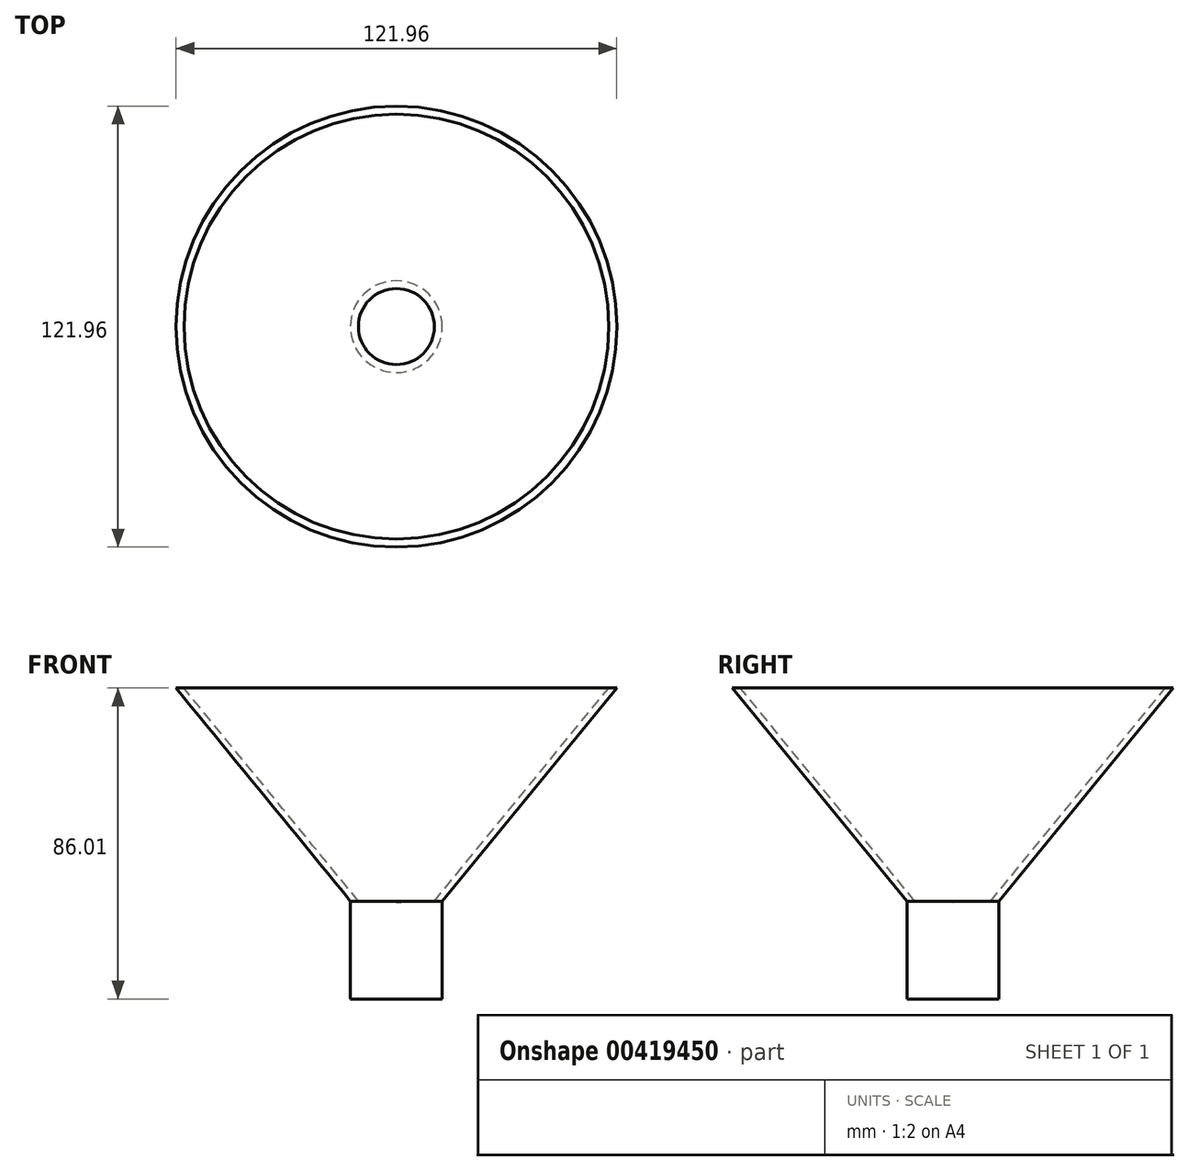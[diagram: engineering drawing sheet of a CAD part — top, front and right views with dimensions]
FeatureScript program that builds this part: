
annotation { "Feature Type Name" : "Feature", "Feature Type Description" : "" }
export const myFeature = defineFeature(function(context is Context, id is Id, definition is map)
    precondition{}
    {
        {
            var Q0;
            Q0=qCreatedBy(makeId("Front.planeOp"),FACE);
            var sketch = newSketch(context, id + "F0", { "sketchPlane" : qUnion([Q0])});
            skLineSegment(sketch, "E0", {"start": v(53.88, 73.08) * mm, "end": v(5.6, 14.12) * mm});
            skLineSegment(sketch, "E1", {"start": v(5.6, 14.12) * mm, "end": v(5.6, -12.93) * mm});
            skLineSegment(sketch, "E2", {"start": v(5.6, -12.93) * mm, "end": v(-7.1, -12.93) * mm});
            skLineSegment(sketch, "E3", {"start": v(-7.1, -12.93) * mm, "end": v(-7.1, 13.84) * mm});
            skLineSegment(sketch, "E4", {"start": v(-7.1, 13.84) * mm, "end": v(3.41, 14.12) * mm});
            skLineSegment(sketch, "E5", {"start": v(3.41, 14.12) * mm, "end": v(51.68, 73.06) * mm});
            skLineSegment(sketch, "E6", {"start": v(51.68, 73.06) * mm, "end": v(53.88, 73.08) * mm});
            skSolve(sketch);
        }
        {
            var Q0;
            Q0=makeQuery(id+"F0.imprint","IMPRINT",FACE,{"disambiguationData":[TD([[makeQuery(id+"F0.imprint","IMPRINT",EDGE,{"derivedFrom":sQuery(id+"F0.wireOp",EDGE,"E0")}),-1.0]])]});
            var Q1;
            Q1=sQuery(id+"F0.wireOp",EDGE,"E3");
            revolve(context, id + "F1", {"entities" : qUnion([Q0]), "axis" : qUnion([Q1]), "revolveType" : RevolveType.FULL});
        }
    });
